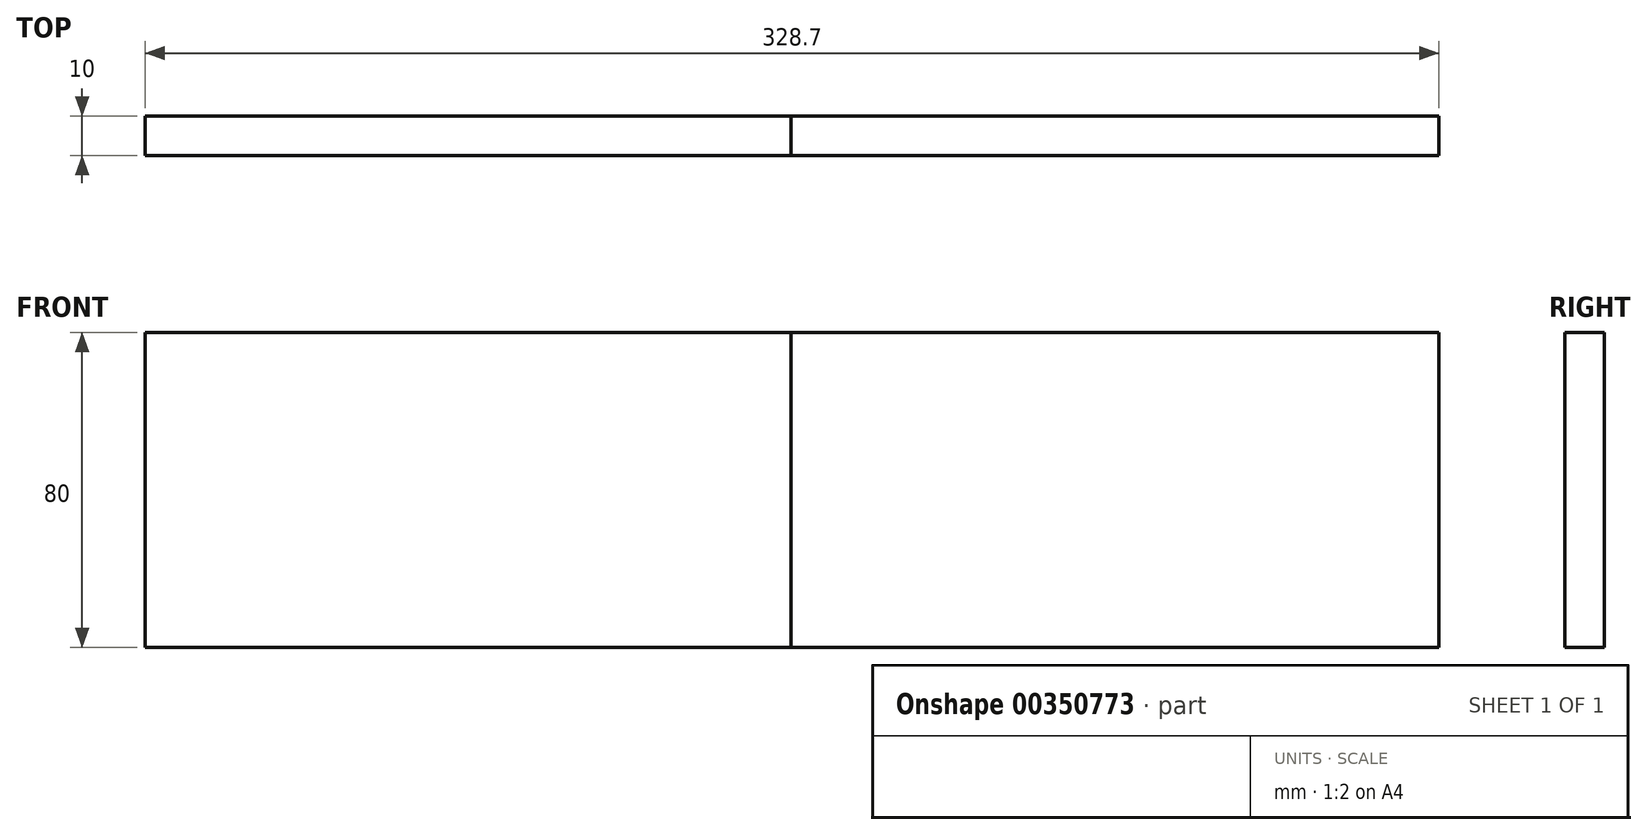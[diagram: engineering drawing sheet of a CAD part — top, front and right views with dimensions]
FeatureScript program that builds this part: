
annotation { "Feature Type Name" : "Feature", "Feature Type Description" : "" }
export const myFeature = defineFeature(function(context is Context, id is Id, definition is map)
    precondition{}
    {
        {
            var Q0;
            Q0=qCreatedBy(makeId("Top.planeOp"),FACE);
            var sketch = newSketch(context, id + "F0", { "sketchPlane" : qUnion([Q0])});
            skLineSegment(sketch, "E0.bottom", {"start": v(167.1, 194) * mm, "end": v(-167.1, 194) * mm});
            skLineSegment(sketch, "E0.top", {"start": v(167.1, -194) * mm, "end": v(-167.1, -194) * mm});
            skLineSegment(sketch, "E0.left", {"start": v(167.1, 194) * mm, "end": v(167.1, -194) * mm});
            skLineSegment(sketch, "E0.right", {"start": v(-167.1, 194) * mm, "end": v(-167.1, -194) * mm});
            skPoint(sketch, "E0.middle", {"position": v(0, 0) * mm});
            skLineSegment(sketch, "E1", {"start": v(-167.1, 194) * mm, "end": v(-167.1, 0) * mm});
            skLineSegment(sketch, "E2", {"start": v(-167.1, 0) * mm, "end": v(-167.1, -194) * mm});
            skLineSegment(sketch, "E3", {"start": v(167.1, -194) * mm, "end": v(167.1, 0) * mm});
            skLineSegment(sketch, "E4", {"start": v(167.1, 0) * mm, "end": v(167.1, 194) * mm});
            skLineSegment(sketch, "E5", {"start": v(-167.1, 0) * mm, "end": v(167.1, 0) * mm});
            skLineSegment(sketch, "E6", {"start": v(-161.1, -188) * mm, "end": v(-161.1, 189) * mm});
            skLineSegment(sketch, "E7", {"start": v(-161.1, 189) * mm, "end": v(162.1, 189) * mm});
            skLineSegment(sketch, "E8", {"start": v(162.1, 189) * mm, "end": v(162.1, -188) * mm});
            skLineSegment(sketch, "E9", {"start": v(162.1, -188) * mm, "end": v(-161.1, -188) * mm});
            skLineSegment(sketch, "E10", {"start": v(-167.1, 0) * mm, "end": v(-161.1, 0) * mm});
            skLineSegment(sketch, "E11", {"start": v(-161.1, 0) * mm, "end": v(162.1, 0) * mm});
            skLineSegment(sketch, "E12", {"start": v(162.1, 0) * mm, "end": v(167.1, 0) * mm});
            skLineSegment(sketch, "E13", {"start": v(164.6, 0) * mm, "end": v(-164.1, 0) * mm});
            skLineSegment(sketch, "E14.bottom", {"start": v(-157.1, 50) * mm, "end": v(-171.1, 50) * mm});
            skLineSegment(sketch, "E14.top", {"start": v(-157.1, -50) * mm, "end": v(-171.1, -50) * mm});
            skLineSegment(sketch, "E14.left", {"start": v(-157.1, 50) * mm, "end": v(-157.1, -50) * mm});
            skLineSegment(sketch, "E14.right", {"start": v(-171.1, 50) * mm, "end": v(-171.1, -50) * mm});
            skPoint(sketch, "E14.middle", {"position": v(-164.1, 0) * mm});
            skLineSegment(sketch, "E15.bottom", {"start": v(171.1, 50) * mm, "end": v(158.1, 50) * mm});
            skLineSegment(sketch, "E15.top", {"start": v(171.1, -50) * mm, "end": v(158.1, -50) * mm});
            skLineSegment(sketch, "E15.left", {"start": v(171.1, 50) * mm, "end": v(171.1, -50) * mm});
            skLineSegment(sketch, "E15.right", {"start": v(158.1, 50) * mm, "end": v(158.1, -50) * mm});
            skPoint(sketch, "E15.middle", {"position": v(164.6, 0) * mm});
            skLineSegment(sketch, "E16.bottom", {"start": v(158.1, 5) * mm, "end": v(162.1, 5) * mm});
            skLineSegment(sketch, "E16.top", {"start": v(158.1, -5) * mm, "end": v(162.1, -5) * mm});
            skLineSegment(sketch, "E16.left", {"start": v(158.1, 5) * mm, "end": v(158.1, -5) * mm});
            skLineSegment(sketch, "E16.right", {"start": v(162.1, 5) * mm, "end": v(162.1, -5) * mm});
            skLineSegment(sketch, "E17.bottom", {"start": v(-157.1, 5) * mm, "end": v(-161.1, 5) * mm});
            skLineSegment(sketch, "E17.top", {"start": v(-157.1, -5) * mm, "end": v(-161.1, -5) * mm});
            skLineSegment(sketch, "E17.left", {"start": v(-157.1, 5) * mm, "end": v(-157.1, -5) * mm});
            skLineSegment(sketch, "E17.right", {"start": v(-161.1, 5) * mm, "end": v(-161.1, -5) * mm});
            skSolve(sketch);
        }
        {
            var Q0;
            Q0=qCreatedBy(makeId("Right.planeOp"),FACE);
            var sketch = newSketch(context, id + "F1", { "sketchPlane" : qUnion([Q0])});
            skLineSegment(sketch, "E18.bottom", {"start": v(5, 0) * mm, "end": v(-5, 0) * mm});
            skLineSegment(sketch, "E18.top", {"start": v(5, 80) * mm, "end": v(-5, 80) * mm});
            skLineSegment(sketch, "E18.left", {"start": v(5, 0) * mm, "end": v(5, 80) * mm});
            skLineSegment(sketch, "E18.right", {"start": v(-5, 0) * mm, "end": v(-5, 80) * mm});
            skSolve(sketch);
        }
        {
            var Q0;
            Q0=makeQuery(id+"F1.imprint","IMPRINT",FACE,{"disambiguationData":[TD([[makeQuery(id+"F1.imprint","IMPRINT",EDGE,{"derivedFrom":sQuery(id+"F1.wireOp",EDGE,"E18.bottom")}),-1.0]])]});
            extrude(context, id + "F2", {"entities" : qUnion([Q0]), "depth" : 164.6 * mm});
        }
        {
            var Q0;
            Q0=makeQuery(id+"F2.opExtrude","CAP_FACE",FACE,{"disambiguationData":[OSD([sQuery(id+"F1.wireOp",EDGE,"E18.bottom"),sQuery(id+"F1.wireOp",EDGE,"E18.top"),sQuery(id+"F1.wireOp",EDGE,"E18.left"),sQuery(id+"F1.wireOp",EDGE,"E18.right")])],"isStart":true});
            extrude(context, id + "F3", {"entities" : qUnion([Q0]), "depth" : 164.1 * mm});
        }
    });
